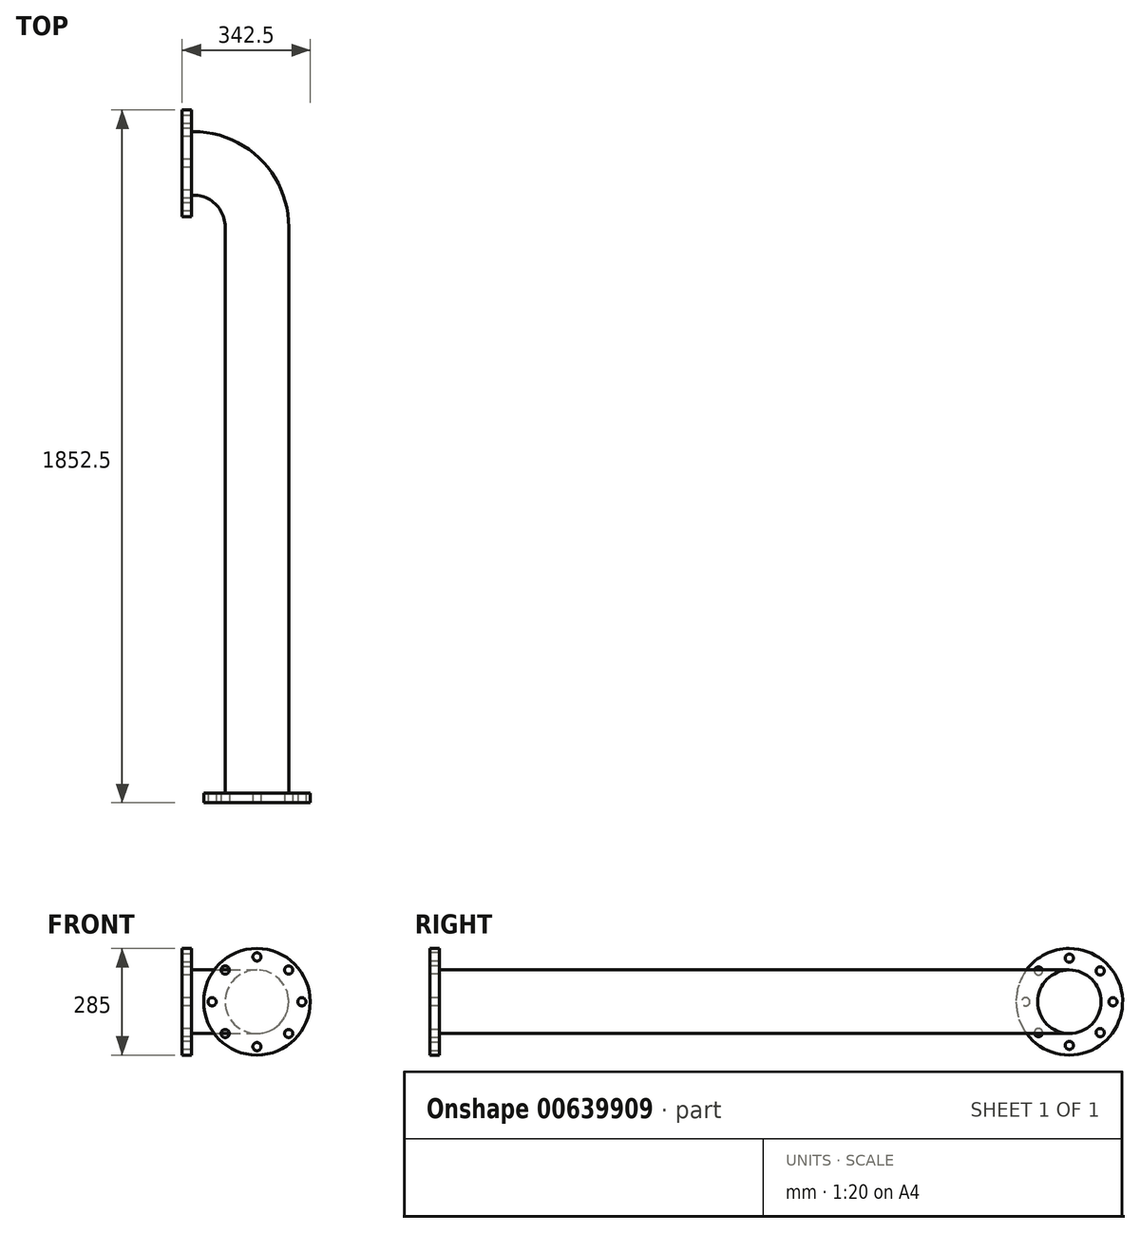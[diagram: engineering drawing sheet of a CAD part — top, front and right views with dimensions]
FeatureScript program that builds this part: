
annotation { "Feature Type Name" : "Feature", "Feature Type Description" : "" }
export const myFeature = defineFeature(function(context is Context, id is Id, definition is map)
    precondition{}
    {
        {
            var Q0;
            Q0=qCreatedBy(makeId("Right.planeOp"),FACE);
            var sketch = newSketch(context, id + "F0", { "sketchPlane" : qUnion([Q0])});
            skCircle(sketch, "E0", {"center": v(0, 0) * mm, "radius": 85 * mm});
            skSolve(sketch);
        }
        {
            var Q0;
            Q0=qCreatedBy(makeId("Top.planeOp"),FACE);
            var sketch = newSketch(context, id + "F1", { "sketchPlane" : qUnion([Q0])});
            skLineSegment(sketch, "E1", {"start": v(0, 0) * mm, "end": v(30, 0) * mm});
            skLineSegment(sketch, "E2", {"start": v(200, -170) * mm, "end": v(200, -1890) * mm});
            skPoint(sketch, "E3.visualSharp", {"position": v(200, 0) * mm});
            skArc(sketch, "E3.filletArc", {"start": v(200, -170) * mm, "mid": v(150.2, -49.8) * mm, "end": v(30, 0) * mm});
            skSolve(sketch);
        }
        {
            var Q0;
            Q0=qCreatedBy(makeId("Right.planeOp"),FACE);
            cPlane(context, id + "F2", {"entities" : qUnion([Q0]), "cplaneType" : CPlaneType.OFFSET, "offset" : 200 * mm, "width" : 150 * mm, "height" : 150 * mm});
        }
        {
            var Q0;
            Q0=qCreatedBy(id+"F2.planeOp",FACE);
            var sketch = newSketch(context, id + "F3", { "sketchPlane" : qUnion([Q0])});
            skLineSegment(sketch, "E4.0", {"start": v(-170, 0) * mm, "end": v(-1710, 0) * mm});
            skLineSegment(sketch, "E5", {"start": v(-1890, 180) * mm, "end": v(-1890, 280) * mm});
            skPoint(sketch, "E6.visualSharp", {"position": v(-1890, 0) * mm});
            skArc(sketch, "E6.filletArc", {"start": v(-1890, 180) * mm, "mid": v(-1837.28, 52.72) * mm, "end": v(-1710, 0) * mm});
            skSolve(sketch);
        }
        {
            var Q0;
            Q0=makeQuery(id+"F0.imprint","IMPRINT",FACE,{"disambiguationData":[TD([[makeQuery(id+"F0.imprint","IMPRINT",EDGE,{"derivedFrom":sQuery(id+"F0.wireOp",EDGE,"E0")}),1.0]])]});
            var Q1;
            Q1=sQuery(id+"F1.wireOp",EDGE,"E1");
            var Q2;
            Q2=sQuery(id+"F1.wireOp",EDGE,"E3.filletArc");
            var Q3;
            Q3=sQuery(id+"F3.wireOp",EDGE,"E4.0");
            sweep(context, id + "F4", {"profiles" : qUnion([Q0]), "path" : qUnion([Q1, Q2, Q3])});
        }
        {
            var Q0;
            Q0=makeQuery(id+"F4.opSweep","CAP_FACE",FACE,{"disambiguationData":[OSD([sQuery(id+"F0.wireOp",EDGE,"E0"),sQuery(id+"F3.wireOp",VERTEX,"E5.end")])],"isStart":false});
            var sketch = newSketch(context, id + "F5", { "sketchPlane" : qUnion([Q0])});
            skCircle(sketch, "E7", {"center": v(200, 0) * mm, "radius": 142.5 * mm});
            skCircle(sketch, "E8", {"center": v(80, 0) * mm, "radius": 11 * mm});
            skCircle(sketch, "E9.1.0", {"center": v(115.15, -84.85) * mm, "radius": 11 * mm});
            skCircle(sketch, "E9.2.0", {"center": v(200, -120) * mm, "radius": 11 * mm});
            skCircle(sketch, "E9.3.0", {"center": v(284.85, -84.85) * mm, "radius": 11 * mm});
            skCircle(sketch, "E9.4.0", {"center": v(320, 0) * mm, "radius": 11 * mm});
            skCircle(sketch, "E9.5.0", {"center": v(284.85, 84.85) * mm, "radius": 11 * mm});
            skCircle(sketch, "E9.6.0", {"center": v(200, 120) * mm, "radius": 11 * mm});
            skCircle(sketch, "E9.7.0", {"center": v(115.15, 84.85) * mm, "radius": 11 * mm});
            skSolve(sketch);
        }
        {
            var Q0;
            Q0=makeQuery(id+"F5.imprint","IMPRINT",FACE,{"disambiguationData":[TD([[makeQuery(id+"F5.imprint","IMPRINT",EDGE,{"derivedFrom":sQuery(id+"F5.wireOp",EDGE,"E7")}),1.0]])]});
            extrude(context, id + "F6", {"entities" : qUnion([Q0]), "operationType" : NewBodyOperationType.ADD, "oppositeDirection" : true, "depth" : 25 * mm, "offsetDistance" : 25 * mm});
        }
        {
            var Q0;
            Q0=makeQuery(id+"F4.opSweep","CAP_FACE",FACE,{"disambiguationData":[OSD([sQuery(id+"F0.wireOp",EDGE,"E0"),sQuery(id+"F1.wireOp",VERTEX,"E1.start")])],"isStart":true});
            var sketch = newSketch(context, id + "F7", { "sketchPlane" : qUnion([Q0])});
            skCircle(sketch, "E10", {"center": v(0, 0) * mm, "radius": 142.5 * mm});
            skCircle(sketch, "E11", {"center": v(0, 116.65) * mm, "radius": 11 * mm});
            skCircle(sketch, "E12.1.0", {"center": v(-82.48, 82.48) * mm, "radius": 11 * mm});
            skCircle(sketch, "E12.2.0", {"center": v(-116.65, 0) * mm, "radius": 11 * mm});
            skCircle(sketch, "E12.3.0", {"center": v(-82.48, -82.48) * mm, "radius": 11 * mm});
            skCircle(sketch, "E12.4.0", {"center": v(0, -116.65) * mm, "radius": 11 * mm});
            skCircle(sketch, "E12.5.0", {"center": v(82.48, -82.48) * mm, "radius": 11 * mm});
            skCircle(sketch, "E12.6.0", {"center": v(116.65, 0) * mm, "radius": 11 * mm});
            skCircle(sketch, "E12.7.0", {"center": v(82.48, 82.48) * mm, "radius": 11 * mm});
            skSolve(sketch);
        }
        {
            var Q0;
            Q0=makeQuery(id+"F7.imprint","IMPRINT",FACE,{"disambiguationData":[TD([[makeQuery(id+"F7.imprint","IMPRINT",EDGE,{"derivedFrom":sQuery(id+"F7.wireOp",EDGE,"E10")}),1.0]])]});
            extrude(context, id + "F8", {"entities" : qUnion([Q0]), "operationType" : NewBodyOperationType.ADD, "oppositeDirection" : true, "depth" : 25 * mm, "offsetDistance" : 25 * mm});
        }
    });
